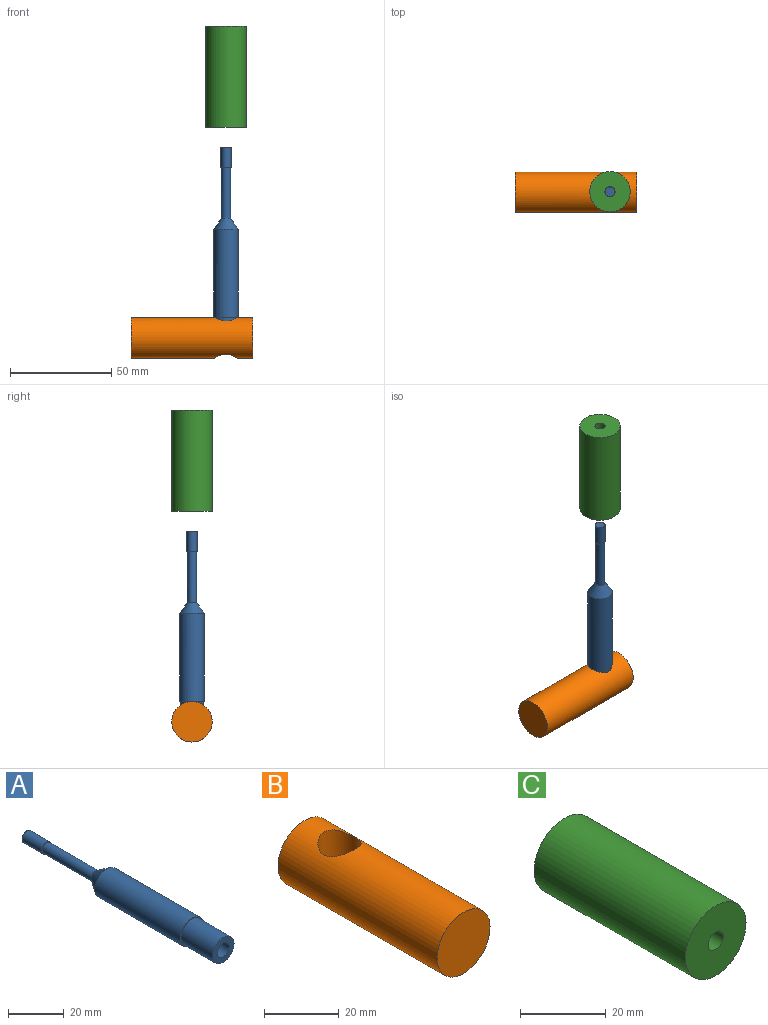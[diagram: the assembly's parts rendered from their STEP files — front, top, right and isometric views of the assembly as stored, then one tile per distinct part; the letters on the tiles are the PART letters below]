
ASSEMBLY  parts=3 mates=2
PART A: 11 faces, bbox 12x100x12 mm
  f0: cylinder r=2.25mm len=25mm, axis (0,-1,0), area 353.4mm2, adj f2,f9
  f1: cylinder r=6mm len=43.5mm, axis (0,1,0), area 1639.9mm2, adj f2,f4
  f2: cone r=2.25mm half-angle=34.3deg, axis (0,-1,0), area 172.5mm2, adj f0,f1
  f3: cylinder r=5.47mm len=16mm, axis (0,-1,0), area 550.4mm2, adj f4,f7
  f4: plane 12x12mm, normal (0,-1,0), area 18.9mm2, adj f1,f3
  f5: plane 6x6mm, normal (0,-1,0), area 28.3mm2, adj f6
  f6: cylinder r=3mm len=28mm, axis (0,-1,0), area 527.8mm2, adj f5,f7
  f7: plane 10.95x10.95mm, normal (0,-1,0), area 65.9mm2, adj f3,f6
  f8: cylinder r=2.48mm len=10mm, axis (0,1,0), area 155.5mm2, adj f9,f10
  f9: plane 4.95x4.95mm, normal (0,-1,0), area 3.3mm2, adj f0,f8
  f10: plane 4.95x4.95mm, normal (0,1,0), area 19.2mm2, adj f8
PART B: 4 faces, bbox 20x60x20 mm
  f0: cylinder r=10mm len=60mm, axis (0,1,0), area 3552.3mm2, adj f1,f2,f3
  f1: plane 20x20mm, normal (0,-1,0), area 314.2mm2, adj f0
  f2: plane 20x20mm, normal (0,1,0), area 314.2mm2, adj f0
  f3: cylinder r=5.75mm len=20mm, axis (0,0,-1), area 658.5mm2, adj f0
PART C: 5 faces, bbox 20x50x20 mm
  f0: cylinder r=10mm len=50mm, axis (0,1,0), area 3141.6mm2, adj f1,f2
  f1: plane 20x20mm, normal (0,-1,0), area 294.5mm2, adj f0,f3
  f2: plane 20x20mm, normal (0,1,0), area 59.7mm2, adj f0,f4
  f3: cylinder r=2.5mm len=45mm, axis (0,-1,0), area 706.9mm2, adj f1,f4
  f4: cone r=9mm half-angle=52.4deg, axis (0,1,0), area 296.3mm2, adj f2,f3
PLACE A rot(axis=(1,0,0),90deg) t=(-82.14,83.96,35.99)mm
PLACE B rot(axis=(0,0,-1),90deg) t=(-68.95,83.96,-23.13)mm
PLACE C rot(axis=(-1,0,0),90deg) t=(-82.14,83.96,80.99)mm fixed
MATE slider A.f8 <-> C.f3  axis (0,0,1) through (-82.14,83.96,70.99)mm
MATE fastened B.f3 <-> A.f1  axis (0,0,-1) through (-82.14,83.96,-13.01)mm
